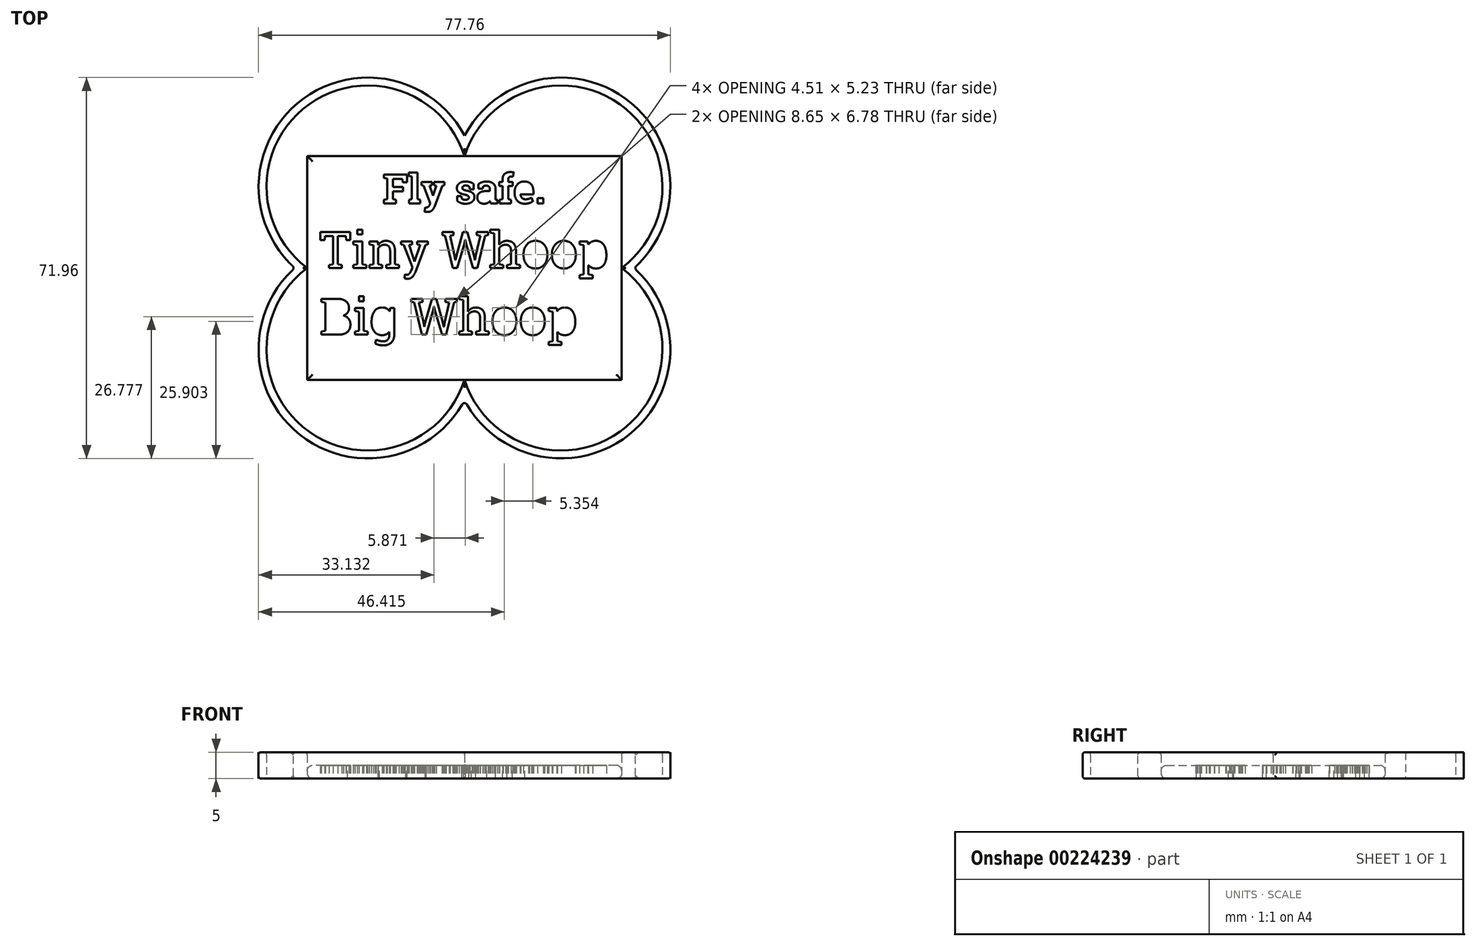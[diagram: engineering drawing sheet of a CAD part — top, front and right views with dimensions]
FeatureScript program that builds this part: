
annotation { "Feature Type Name" : "Feature", "Feature Type Description" : "" }
export const myFeature = defineFeature(function(context is Context, id is Id, definition is map)
    precondition{}
    {
        {
            var Q0;
            Q0=qCreatedBy(makeId("Top.planeOp"),FACE);
            var sketch = newSketch(context, id + "F0", { "sketchPlane" : qUnion([Q0])});
            skLineSegment(sketch, "E0.bottom", {"start": v(29.68, -21.15) * mm, "end": v(-29.68, -21.15) * mm});
            skLineSegment(sketch, "E0.top", {"start": v(29.68, 21.15) * mm, "end": v(-29.68, 21.15) * mm});
            skLineSegment(sketch, "E0.left", {"start": v(29.68, -21.15) * mm, "end": v(29.68, 21.15) * mm});
            skLineSegment(sketch, "E0.right", {"start": v(-29.68, -21.15) * mm, "end": v(-29.68, 21.15) * mm});
            skPoint(sketch, "E0.middle", {"position": v(0, 0) * mm});
            skText(sketch, "E1", { "text": "Tiny Whoop \nBig Whoop", "fontName": "RobotoSlab-Regular.ttf"});
            skText(sketch, "E2", { "text": "Fly safe. ", "fontName": "RobotoSlab-Bold.ttf"});
            skArc(sketch, "E3", {"start": v(0, 21.15) * mm, "mid": v(-29.34, 30.93) * mm, "end": v(-29.68, 0) * mm});
            skArc(sketch, "E4.MirrorCS", {"start": v(0, 21.15) * mm, "mid": v(29.34, 30.93) * mm, "end": v(29.68, 0) * mm});
            skArc(sketch, "E5.MirrorCS", {"start": v(0, -21.15) * mm, "mid": v(29.34, -30.93) * mm, "end": v(29.68, 0) * mm});
            skArc(sketch, "E6.MirrorCS", {"start": v(0, -21.15) * mm, "mid": v(-29.34, -30.93) * mm, "end": v(-29.68, 0) * mm});
            skArc(sketch, "E7.0", {"start": v(0, 25) * mm, "mid": v(-30.93, 31.61) * mm, "end": v(-32.04, 0) * mm});
            skArc(sketch, "E7.1", {"start": v(0, 25) * mm, "mid": v(30.93, 31.61) * mm, "end": v(32.04, 0) * mm});
            skArc(sketch, "E7.2", {"start": v(0, -25) * mm, "mid": v(30.93, -31.61) * mm, "end": v(32.04, 0) * mm});
            skArc(sketch, "E7.3", {"start": v(0, -25) * mm, "mid": v(-30.93, -31.61) * mm, "end": v(-32.04, 0) * mm});
            const initialGuessF0  = {"E1": [-0.02737, 0, 1, 0, 0.00687], "E2": [-0.0154, 0.01222, 1, 0, 0.00552]};
            skSetInitialGuess(sketch, initialGuessF0);
            skSolve(sketch);
        }
        {
            var Q0;
            Q0=makeQuery(id+"F0.imprint","IMPRINT",FACE,{"disambiguationData":[TD([[makeQuery(id+"F0.imprint","IMPRINT",EDGE,{"derivedFrom":sQuery(id+"F0.wireOp",EDGE,"E0.bottom")}),-1.0]])]});
            extrude(context, id + "F1", {"entities" : qUnion([Q0]), "depth" : 2.5 * mm});
        }
        {
            var Q0;
            Q0 = qSketchRegion(id + "F0", true);
            extrude(context, id + "F2", {"entities" : qUnion([Q0]), "operationType" : NewBodyOperationType.ADD, "depth" : 5 * mm});
        }
        {
            var Q0;
            Q0=makeQuery(id+"F2.opExtrude","SWEPT_FACE",FACE,{"disambiguationData":[OSD([sQuery(id+"F0.wireOp",EDGE,"E7.2")])]});
            var Q1;
            Q1=makeQuery(id+"F2.opExtrude","SWEPT_FACE",FACE,{"disambiguationData":[OSD([sQuery(id+"F0.wireOp",EDGE,"E7.3")])]});
            fillet(context, id + "F3", {"entities" : qUnion([Q0, Q1]), "radius" : 0.5 * mm, "tangentPropagation" : true, "allowEdgeOverflow" : false});
        }
        {
            var Q0;
            Q0=makeQuery(id+"F2.opExtrude","CAP_EDGE",EDGE,{"disambiguationData":[OSD([sQuery(id+"F0.wireOp",EDGE,"E3")])],"isStart":false});
            var Q1;
            Q1=makeQuery(id+"F2.opExtrude","CAP_EDGE",EDGE,{"disambiguationData":[OSD([sQuery(id+"F0.wireOp",EDGE,"E6.MirrorCS")])],"isStart":false});
            var Q2;
            Q2=makeQuery(id+"F2.opExtrude","CAP_EDGE",EDGE,{"disambiguationData":[OSD([sQuery(id+"F0.wireOp",EDGE,"E4.MirrorCS")])],"isStart":false});
            var Q3;
            Q3=makeQuery(id+"F2.opExtrude","CAP_EDGE",EDGE,{"disambiguationData":[OSD([sQuery(id+"F0.wireOp",EDGE,"E5.MirrorCS")])],"isStart":false});
            fillet(context, id + "F4", {"entities" : qUnion([Q0, Q1, Q2, Q3]), "radius" : 0.5 * mm, "tangentPropagation" : true, "allowEdgeOverflow" : false});
        }
        {
            var Q0;
            Q0=makeQuery(id+"F1.opExtrude","CAP_EDGE",EDGE,{"disambiguationData":[OSD([sQuery(id+"F0.wireOp",EDGE,"E0.right")])],"isStart":false});
            var Q1;
            Q1=makeQuery(id+"F1.opExtrude","CAP_EDGE",EDGE,{"disambiguationData":[OSD([sQuery(id+"F0.wireOp",EDGE,"E0.bottom")])],"isStart":false});
            var Q2;
            Q2=makeQuery(id+"F1.opExtrude","CAP_EDGE",EDGE,{"disambiguationData":[OSD([sQuery(id+"F0.wireOp",EDGE,"E0.top")])],"isStart":false});
            var Q3;
            Q3=makeQuery(id+"F1.opExtrude","CAP_EDGE",EDGE,{"disambiguationData":[OSD([sQuery(id+"F0.wireOp",EDGE,"E0.left")])],"isStart":false});
            fillet(context, id + "F5", {"entities" : qUnion([Q0, Q1, Q2, Q3]), "radius" : 1 * mm, "tangentPropagation" : true, "allowEdgeOverflow" : false});
        }
        {
            var Q0;
            Q0=makeQuery(id+"F1.opExtrude","CAP_EDGE",EDGE,{"disambiguationData":[OSD([sQuery(id+"F0.wireOp",EDGE,"E0.left")])],"isStart":true});
            var Q1;
            Q1=makeQuery(id+"F1.opExtrude","CAP_EDGE",EDGE,{"disambiguationData":[OSD([sQuery(id+"F0.wireOp",EDGE,"E0.bottom")])],"isStart":true});
            var Q2;
            Q2=makeQuery(id+"F1.opExtrude","CAP_EDGE",EDGE,{"disambiguationData":[OSD([sQuery(id+"F0.wireOp",EDGE,"E0.top")])],"isStart":true});
            var Q3;
            Q3=makeQuery(id+"F1.opExtrude","CAP_EDGE",EDGE,{"disambiguationData":[OSD([sQuery(id+"F0.wireOp",EDGE,"E0.right")])],"isStart":true});
            fillet(context, id + "F6", {"entities" : qUnion([Q0, Q1, Q2, Q3]), "radius" : 1 * mm, "tangentPropagation" : true, "allowEdgeOverflow" : false});
        }
    });
